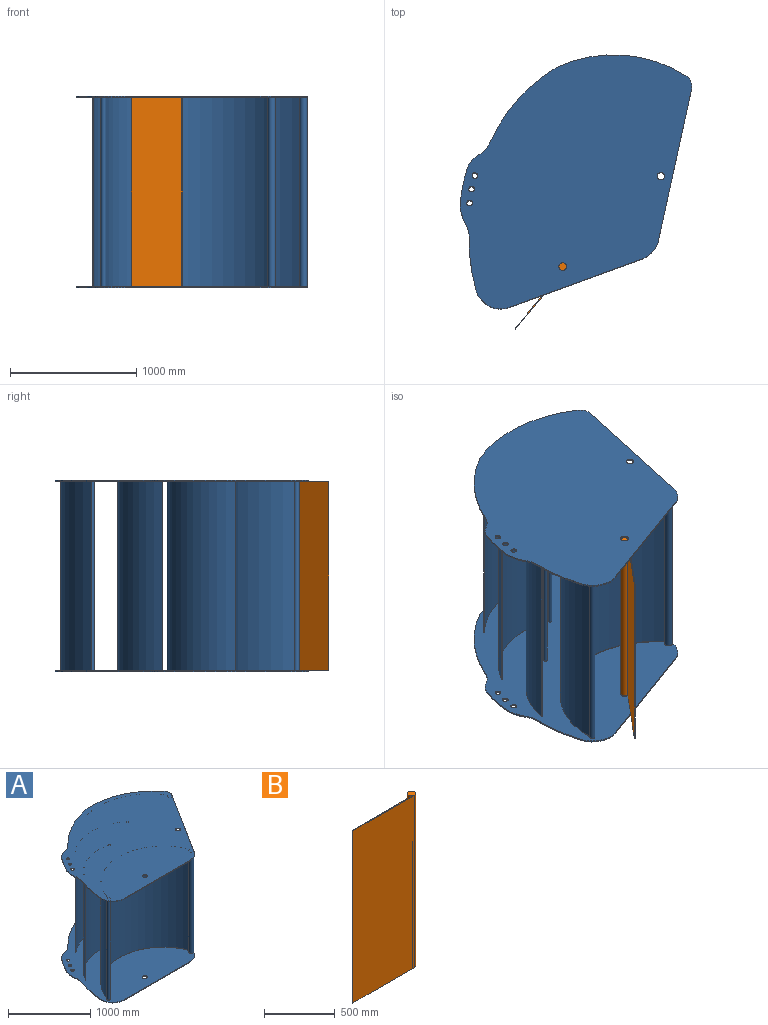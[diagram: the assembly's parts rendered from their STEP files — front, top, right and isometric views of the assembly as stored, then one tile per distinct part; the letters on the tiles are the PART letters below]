
ASSEMBLY  parts=2 mates=2
PART A: 61 faces, bbox 2164.2x1661x1520 mm
  f0: cylinder r=30.5mm len=61mm, axis (0,0,-1), area 1916.4mm2, adj f48,f49
  f1: cylinder r=29.5mm len=59mm, axis (0,0,-1), area 1853.5mm2, adj f48,f49
  f2: cylinder r=22mm len=44mm, axis (0,0,-1), area 1382.3mm2, adj f48,f49
  f3: cylinder r=22mm len=44mm, axis (0,0,-1), area 1382.3mm2, adj f48,f49
  f4: cylinder r=22mm len=44mm, axis (0,0,-1), area 1382.3mm2, adj f48,f49
  f5: cylinder r=326.18mm len=176.61mm, axis (0,0,-1), area 1797.7mm2, adj f48,f49,f50,f60
  f6: cylinder r=200mm len=212.82mm, axis (0,0,-1), area 3269.9mm2, adj f48,f49,f51,f52
  f7: cylinder r=20.5mm len=1500mm, axis (0,0,-1), area 183146.8mm2, adj f30,f44,f45,f49
  f8: cylinder r=30.5mm len=1500mm, axis (0,0,-1), area 272705.4mm2, adj f30,f44,f45,f46,f47,f49
  f9: cylinder r=15.5mm len=1500mm, axis (0,0,-1), area 135747.8mm2, adj f30,f41,f43,f49
  f10: cylinder r=15.5mm len=1500mm, axis (0,0,-1), area 136340.4mm2, adj f30,f37,f40,f49
  f11: cylinder r=30.5mm len=1500mm, axis (0,0,-1), area 274743.1mm2, adj f30,f32,f34,f35,f36,f49
  f12: cylinder r=30.5mm len=61mm, axis (0,0,-1), area 1916.4mm2, adj f30,f31
  f13: cylinder r=22mm len=44mm, axis (0,0,-1), area 1382.3mm2, adj f30,f31
  f14: cylinder r=22mm len=44mm, axis (0,0,-1), area 1382.3mm2, adj f30,f31
  f15: cylinder r=22mm len=44mm, axis (0,0,-1), area 1382.3mm2, adj f30,f31
  f16: cylinder r=29.5mm len=59mm, axis (0,0,-1), area 1853.5mm2, adj f30,f31
  f17: cylinder r=326.18mm len=176.61mm, axis (0,0,-1), area 1797.7mm2, adj f28,f29,f30,f31
  f18: cylinder r=200mm len=212.82mm, axis (0,0,-1), area 3269.9mm2, adj f19,f20,f30,f31
  f19: cylinder r=1403.06mm len=415.74mm, axis (0,0,-1), area 4273.2mm2, adj f18,f29,f30,f31
  f20: plane 1123.76x10mm, normal (0,-1,0), area 11237.6mm2, adj f18,f21,f30,f31
  f21: cylinder r=200mm len=169mm, axis (0,0,-1), area 2013.2mm2, adj f20,f22,f30,f31
  f22: plane 1036.5x655.9mm, normal (0.85,-0.53,0), area 12265.9mm2, adj f21,f23,f30,f31,f36,f47
  f23: cylinder r=100mm len=114.68mm, axis (0,0,-1), area 1222.9mm2, adj f22,f24,f30,f31
  f24: cylinder r=1074.34mm len=926.41mm, axis (0,0,-1), area 10568mm2, adj f23,f25,f30,f31
  f25: cylinder r=1282.61mm len=713.26mm, axis (0,0,-1), area 8227.7mm2, adj f24,f26,f30,f31
  f26: cylinder r=200mm len=117.51mm, axis (0,0,-1), area 1346.6mm2, adj f25,f27,f30,f31
  f27: cylinder r=186.95mm len=116.81mm, axis (0,0,-1), area 1363.1mm2, adj f26,f28,f30,f31
  f28: cylinder r=1324.47mm len=239.75mm, axis (0,0,-1), area 2828.3mm2, adj f17,f27,f30,f31
  f29: cylinder r=200mm len=107.43mm, axis (0,0,-1), area 1093.1mm2, adj f17,f19,f30,f31
  f30: plane 2164.16x1660.98mm, normal (0,0,1), area 2565292.9mm2, adj f7,f8,f9,f10,f11,f12,f13,f14
  f31: plane 2164.16x1660.98mm, normal (0,0,-1), area 2603609.2mm2, adj f12,f13,f14,f15,f16,f17,f18,f19
  f32: cylinder r=883.17mm len=1500mm, axis (0,0,-1), area 1936048.7mm2, adj f11,f30,f33,f49
  f33: plane 1500x5.5mm, normal (-0.92,-0.4,0), area 9000mm2, adj f30,f32,f34,f49
  f34: cylinder r=877.17mm len=1500mm, axis (0,0,-1), area 1914005.6mm2, adj f11,f30,f33,f49
  f35: plane 9.3x5.88mm, normal (0,0,1), area 3.7mm2, adj f11,f54
  f36: plane 9.3x5.88mm, normal (0,0,-1), area 3.7mm2, adj f11,f22
  f37: cylinder r=685.89mm len=1500mm, axis (0,0,-1), area 1444091.5mm2, adj f10,f30,f38,f49
  f38: plane 1500x4.62mm, normal (-0.77,-0.64,0), area 9000mm2, adj f30,f37,f39,f49
  f39: plane 1500x0.08mm, normal (0.65,-0.76,0), area 152.6mm2, adj f30,f38,f40,f49
  f40: cylinder r=679.89mm len=1500mm, axis (0,0,-1), area 1427930.9mm2, adj f10,f30,f39,f49
  f41: cylinder r=640.37mm len=1500mm, axis (0,0,-1), area 1242581.2mm2, adj f9,f30,f42,f49
  f42: plane 1500x5.24mm, normal (-0.49,-0.87,0), area 9000mm2, adj f30,f41,f43,f49
  f43: cylinder r=634.37mm len=1500mm, axis (0,0,-1), area 1226053.6mm2, adj f9,f30,f42,f49
  f44: cylinder r=755.25mm len=1500mm, axis (0,0,-1), area 2799788.5mm2, adj f7,f8,f30,f49
  f45: cylinder r=761.25mm len=1500mm, axis (0,0,-1), area 2838096.4mm2, adj f7,f8,f30,f49
  f46: plane 9.3x5.88mm, normal (0,0,1), area 3.7mm2, adj f8,f54
  f47: plane 9.3x5.88mm, normal (0,0,-1), area 3.7mm2, adj f8,f22
  f48: plane 2164.16x1660.98mm, normal (0,0,1), area 2603609.2mm2, adj f0,f1,f2,f3,f4,f5,f6,f50
  f49: plane 2164.16x1660.98mm, normal (0,0,-1), area 2565292.9mm2, adj f0,f1,f2,f3,f4,f5,f6,f7
  f50: cylinder r=200mm len=107.43mm, axis (0,0,-1), area 1093.1mm2, adj f5,f48,f49,f51
  f51: cylinder r=1403.06mm len=415.74mm, axis (0,0,-1), area 4273.2mm2, adj f6,f48,f49,f50
  f52: plane 1123.76x10mm, normal (0,-1,0), area 11237.6mm2, adj f6,f48,f49,f53
  f53: cylinder r=200mm len=169mm, axis (0,0,-1), area 2013.2mm2, adj f48,f49,f52,f54
  f54: plane 1036.5x655.9mm, normal (0.85,-0.53,0), area 12265.9mm2, adj f35,f46,f48,f49,f53,f55
  f55: cylinder r=100mm len=114.68mm, axis (0,0,-1), area 1222.9mm2, adj f48,f49,f54,f56
  f56: cylinder r=1074.34mm len=926.41mm, axis (0,0,-1), area 10568mm2, adj f48,f49,f55,f57
  f57: cylinder r=1282.61mm len=713.26mm, axis (0,0,-1), area 8227.7mm2, adj f48,f49,f56,f58
  f58: cylinder r=200mm len=117.51mm, axis (0,0,-1), area 1346.6mm2, adj f48,f49,f57,f59
  f59: cylinder r=186.95mm len=116.81mm, axis (0,0,-1), area 1363.1mm2, adj f48,f49,f58,f60
  f60: cylinder r=1324.47mm len=239.75mm, axis (0,0,-1), area 2828.3mm2, adj f5,f48,f49,f59
PART B: 6 faces, bbox 646.3x61x1490 mm
  f0: cylinder r=30.5mm len=1490mm, axis (0,0,-1), area 256544.7mm2, adj f1,f2,f4,f5
  f1: plane 1490x615.77mm, normal (0,-1,0), area 917501.9mm2, adj f0,f3,f4,f5
  f2: plane 1490x597.61mm, normal (0,1,0), area 890434.7mm2, adj f0,f3,f4,f5
  f3: plane 1490x6mm, normal (-1,0,0), area 8940mm2, adj f1,f2,f4,f5
  f4: plane 646.27x61mm, normal (0,0,1), area 6542.9mm2, adj f0,f1,f2,f3
  f5: plane 646.27x61mm, normal (0,0,-1), area 6542.9mm2, adj f0,f1,f2,f3
PLACE A rot(axis=(0,0,1),20deg) t=(0,0,-10)mm
PLACE B rot(axis=(0,0,1),50deg) t=(-462.48,292.59,-10)mm
MATE planar A.f0 <-> B.f0  axis (0,0,-1) through (-777.23,-716.71,750)mm
MATE revolute A.f0 <-> B.f0  axis (0,0,-1) through (-777.23,-716.71,750)mm
